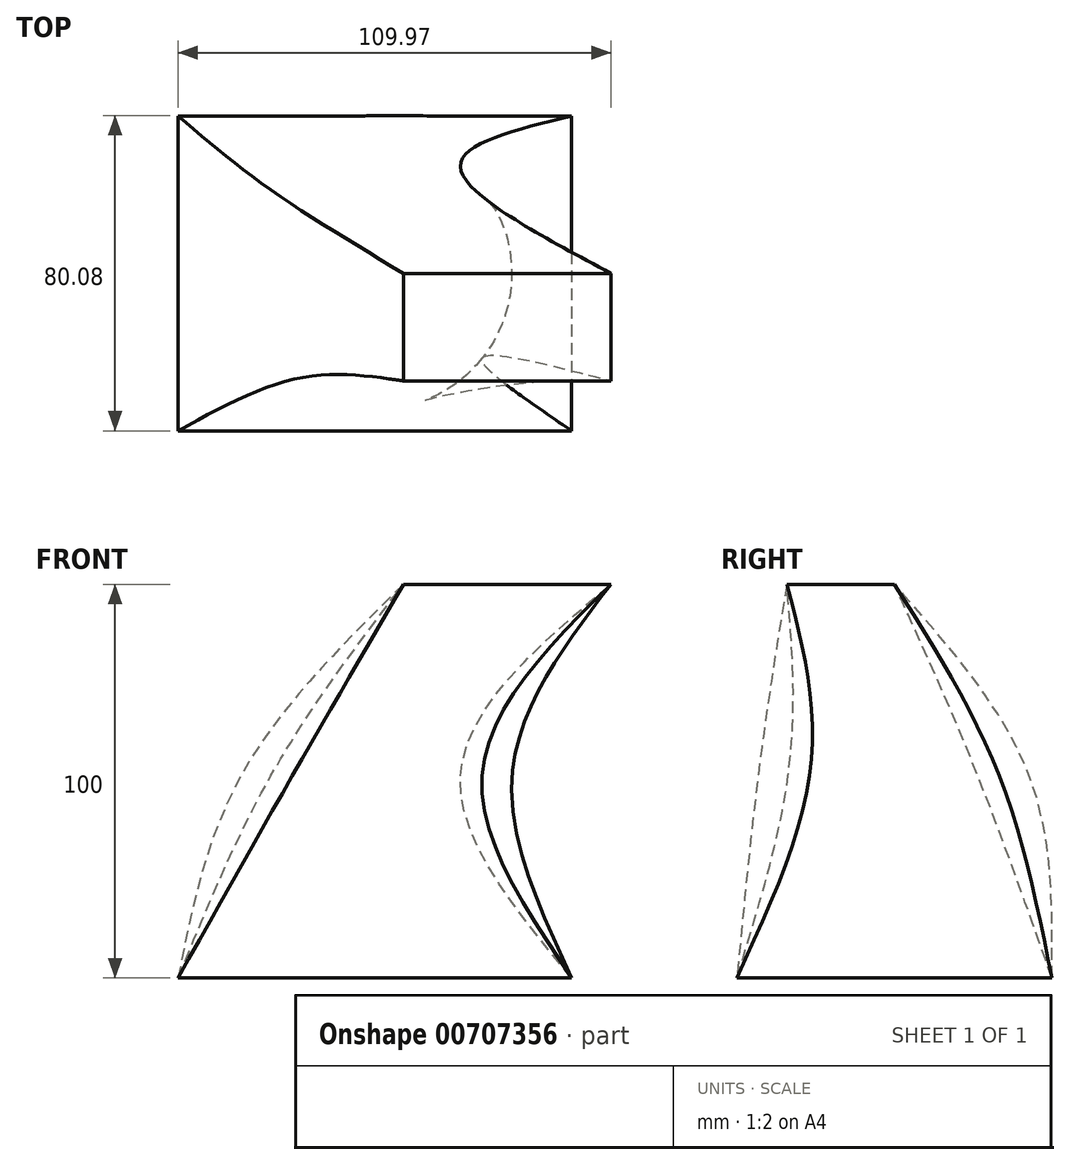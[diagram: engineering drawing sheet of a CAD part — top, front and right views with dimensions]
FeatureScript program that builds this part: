
annotation { "Feature Type Name" : "Feature", "Feature Type Description" : "" }
export const myFeature = defineFeature(function(context is Context, id is Id, definition is map)
    precondition{}
    {
        {
            var Q0;
            Q0=qCreatedBy(makeId("Top.planeOp"),FACE);
            var sketch = newSketch(context, id + "F0", { "sketchPlane" : qUnion([Q0])});
            skLineSegment(sketch, "E0.bottom", {"start": v(-50, 40) * mm, "end": v(50, 40) * mm});
            skLineSegment(sketch, "E0.top", {"start": v(-50, -40) * mm, "end": v(50, -40) * mm});
            skLineSegment(sketch, "E0.left", {"start": v(-50, 40) * mm, "end": v(-50, -40) * mm});
            skLineSegment(sketch, "E0.right", {"start": v(50, 40) * mm, "end": v(50, -40) * mm});
            skSolve(sketch);
        }
        {
            var Q0;
            Q0=qCreatedBy(makeId("Top.planeOp"),FACE);
            cPlane(context, id + "F1", {"entities" : qUnion([Q0]), "cplaneType" : CPlaneType.OFFSET, "offset" : 50 * mm, "width" : 150 * mm, "height" : 150 * mm});
        }
        {
            var Q0;
            Q0=qCreatedBy(id+"F1.planeOp",FACE);
            var sketch = newSketch(context, id + "F2", { "sketchPlane" : qUnion([Q0])});
            skCircle(sketch, "E1", {"center": v(0, 0) * mm, "radius": 34.78 * mm});
            skSolve(sketch);
        }
        {
            var Q0;
            Q0=qCreatedBy(id+"F1.planeOp",FACE);
            cPlane(context, id + "F3", {"entities" : qUnion([Q0]), "cplaneType" : CPlaneType.OFFSET, "offset" : 50 * mm, "width" : 150 * mm, "height" : 150 * mm});
        }
        {
            var Q0;
            Q0=qCreatedBy(id+"F3.planeOp",FACE);
            var sketch = newSketch(context, id + "F4", { "sketchPlane" : qUnion([Q0])});
            skLineSegment(sketch, "E2.bottom", {"start": v(7.24, 0) * mm, "end": v(59.97, 0) * mm});
            skLineSegment(sketch, "E2.top", {"start": v(7.24, -27.32) * mm, "end": v(59.97, -27.32) * mm});
            skLineSegment(sketch, "E2.left", {"start": v(7.24, 0) * mm, "end": v(7.24, -27.32) * mm});
            skLineSegment(sketch, "E2.right", {"start": v(59.97, 0) * mm, "end": v(59.97, -27.32) * mm});
            skSolve(sketch);
        }
        {
            var Q0;
            Q0=makeQuery(id+"F0.imprint","IMPRINT",FACE,{"disambiguationData":[TD([[makeQuery(id+"F0.imprint","IMPRINT",EDGE,{"derivedFrom":sQuery(id+"F0.wireOp",EDGE,"E0.bottom")}),-1.0]])]});
            var Q1;
            Q1 = qSketchRegion(id + "F2", true);
            var Q2;
            Q2 = qSketchRegion(id + "F4", true);
            loft(context, id + "F5", {"sheetProfilesArray" : [{ "sheetProfileEntities" : qUnion([Q0]) }, { "sheetProfileEntities" : qUnion([Q1]) }, { "sheetProfileEntities" : qUnion([Q2]) }]});
        }
    });
